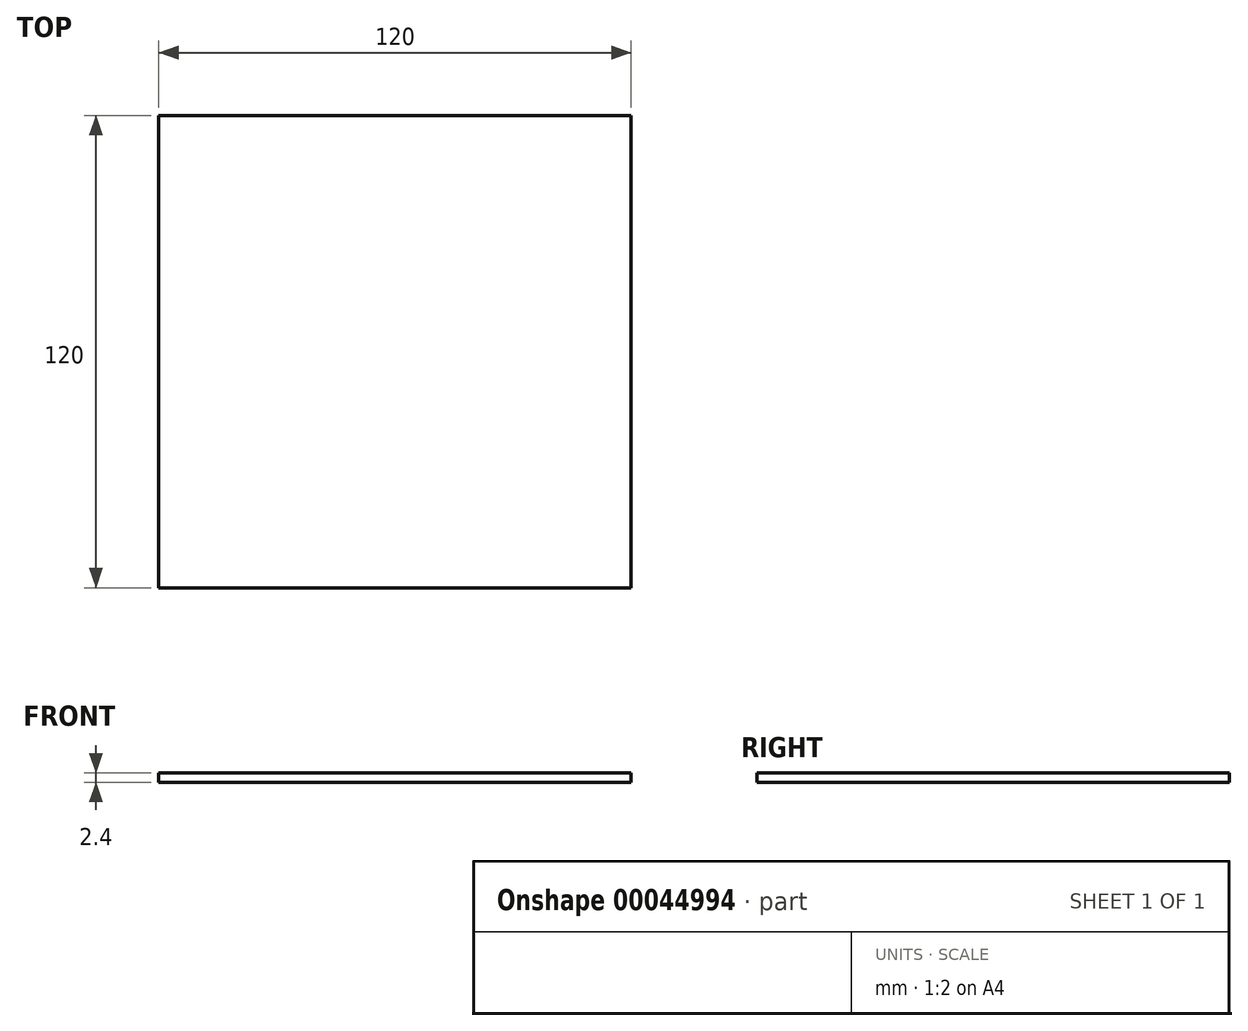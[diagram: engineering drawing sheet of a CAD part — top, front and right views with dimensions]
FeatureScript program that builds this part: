
annotation { "Feature Type Name" : "Feature", "Feature Type Description" : "" }
export const myFeature = defineFeature(function(context is Context, id is Id, definition is map)
    precondition{}
    {
        {
            var Q0;
            Q0=qCreatedBy(makeId("Top.planeOp"),FACE);
            var sketch = newSketch(context, id + "F0", { "sketchPlane" : qUnion([Q0])});
            skLineSegment(sketch, "E0.rect.bottom", {"start": v(-60, 60) * mm, "end": v(60, 60) * mm});
            skLineSegment(sketch, "E0.rect.top", {"start": v(-60, -60) * mm, "end": v(60, -60) * mm});
            skLineSegment(sketch, "E0.rect.left", {"start": v(-60, 60) * mm, "end": v(-60, -60) * mm});
            skLineSegment(sketch, "E0.rect.right", {"start": v(60, 60) * mm, "end": v(60, -60) * mm});
            skPoint(sketch, "E0.rect.middle", {"position": v(0, 0) * mm});
            skSolve(sketch);
        }
        {
            var Q0;
            Q0=makeQuery(id+"F0.imprint","IMPRINT",FACE,{"disambiguationData":[TD([[makeQuery(id+"F0.imprint","IMPRINT",EDGE,{"derivedFrom":sQuery(id+"F0.wireOp",EDGE,"E0.rect.bottom")}),-1.0]])]});
            extrude(context, id + "F1", {"entities" : qUnion([Q0]), "depth" : 2.4 * mm});
        }
    });
